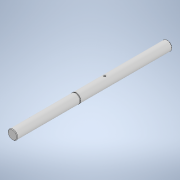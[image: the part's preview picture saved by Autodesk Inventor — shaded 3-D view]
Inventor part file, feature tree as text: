
AUTODESK INVENTOR PART (.ipt)
format: ipt  version: 2022 (Build 260153000, 153)  size: 128,000 bytes
history: native  units: mm
features: sketch x2, other x1, hole x1, extrude x1, projected_geometry x1
ambient origin geometry x8: Origin, YZ Plane, XZ Plane, XY Plane, X Axis, Y Axis, Z Axis, Center Point
bodies: Solid1 (feature_tree)
feature tree (6):
  other  "Shaft"
  hole  "Hole for pin"  [1 undecoded]
  extrude  "Pinhole"  Depth=0.5mm
  sketch  "Sketch1"  dims[d0=120.0mm d2=1.5mm]
  sketch  "Sketch2"  dims[d3=0.5mm d4=0.5mm d5=135.0deg d6=9.0mm d8=175.0mm d9=1.414mm d10=8.0mm d11=360.0deg d12=9.0mm d13=50.0mm d14=3.5mm d15=5.0mm d16=0.0mm d17=0.0mm]
  projected_geometry  "Projected Loop1"
note: 1 required parameter value undecoded (feature->parameter linkage not recoverable at this tier; creation-order binding heuristic only, values carry confidence <= 0.55)
